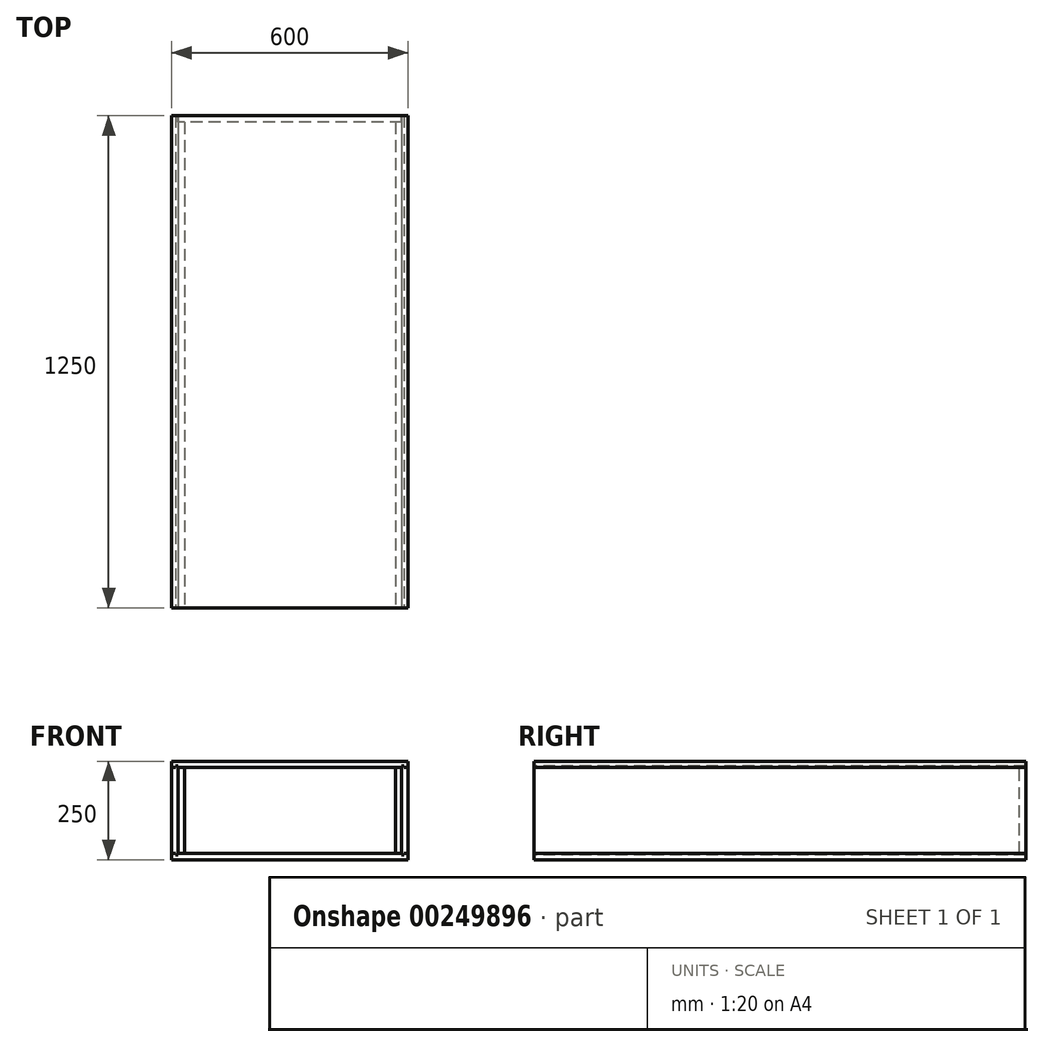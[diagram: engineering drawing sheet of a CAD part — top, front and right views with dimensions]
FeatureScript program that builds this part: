
annotation { "Feature Type Name" : "Feature", "Feature Type Description" : "" }
export const myFeature = defineFeature(function(context is Context, id is Id, definition is map)
    precondition{}
    {
        {
            var Q0;
            Q0=qCreatedBy(makeId("Front.planeOp"),FACE);
            var sketch = newSketch(context, id + "F0", { "sketchPlane" : qUnion([Q0])});
            skLineSegment(sketch, "E0.bottom", {"start": v(300, -125) * mm, "end": v(-300, -125) * mm});
            skLineSegment(sketch, "E0.top", {"start": v(300, 125) * mm, "end": v(-300, 125) * mm});
            skLineSegment(sketch, "E0.left", {"start": v(300, -125) * mm, "end": v(300, 125) * mm});
            skLineSegment(sketch, "E0.right", {"start": v(-300, -125) * mm, "end": v(-300, 125) * mm});
            skPoint(sketch, "E0.middle", {"position": v(0, 0) * mm});
            skLineSegment(sketch, "E1.0", {"start": v(284, 109) * mm, "end": v(-284, 109) * mm});
            skLineSegment(sketch, "E1.1", {"start": v(284, -109) * mm, "end": v(284, 109) * mm});
            skLineSegment(sketch, "E1.2", {"start": v(284, -109) * mm, "end": v(-284, -109) * mm});
            skLineSegment(sketch, "E1.3", {"start": v(-284, -109) * mm, "end": v(-284, 109) * mm});
            skLineSegment(sketch, "E2", {"start": v(284, -109) * mm, "end": v(284, -113) * mm});
            skLineSegment(sketch, "E3", {"start": v(284, -113) * mm, "end": v(290, -113) * mm});
            skLineSegment(sketch, "E4", {"start": v(290, -113) * mm, "end": v(290, -109) * mm});
            skLineSegment(sketch, "E5", {"start": v(290, -109) * mm, "end": v(300, -109) * mm});
            skLineSegment(sketch, "E6", {"start": v(284, 109) * mm, "end": v(284, 113) * mm});
            skLineSegment(sketch, "E7", {"start": v(284, 113) * mm, "end": v(290, 113) * mm});
            skLineSegment(sketch, "E8", {"start": v(290, 113) * mm, "end": v(290, 109) * mm});
            skLineSegment(sketch, "E9", {"start": v(290, 109) * mm, "end": v(300, 109) * mm});
            skLineSegment(sketch, "E10", {"start": v(-284, 109) * mm, "end": v(-284, 113) * mm});
            skLineSegment(sketch, "E11", {"start": v(-284, 113) * mm, "end": v(-290, 113) * mm});
            skLineSegment(sketch, "E12", {"start": v(-290, 113) * mm, "end": v(-290, 109) * mm});
            skLineSegment(sketch, "E13", {"start": v(-290, 109) * mm, "end": v(-300, 109) * mm});
            skLineSegment(sketch, "E14", {"start": v(-284, -109) * mm, "end": v(-284, -113) * mm});
            skLineSegment(sketch, "E15", {"start": v(-284, -113) * mm, "end": v(-290, -113) * mm});
            skLineSegment(sketch, "E16", {"start": v(-290, -113) * mm, "end": v(-290, -109) * mm});
            skLineSegment(sketch, "E17", {"start": v(-290, -109) * mm, "end": v(-300, -109) * mm});
            skLineSegment(sketch, "E18.0", {"start": v(268, -109) * mm, "end": v(268, 109) * mm});
            skLineSegment(sketch, "E19.0", {"start": v(-268, -109) * mm, "end": v(-268, 109) * mm});
            skSolve(sketch);
        }
        {
            var Q0;
            Q0=makeQuery(id+"F0.imprint","IMPRINT",FACE,{"disambiguationData":[TD([[makeQuery(id+"F0.imprint","IMPRINT",EDGE,{"derivedFrom":sQuery(id+"F0.wireOp",EDGE,"E1.1")}),-1.0]])]});
            extrude(context, id + "F1", {"entities" : qUnion([Q0]), "oppositeDirection" : true, "depth" : 1250 * mm});
        }
        {
            var Q0;
            {var subQ7=sQuery(id+"F0.wireOp",EDGE,"E0.top");Q0=makeQuery(id+"F0.imprint","IMPRINT",FACE,{"disambiguationData":[TD([[makeQuery(id+"F0.imprint","IMPRINT",EDGE,{"derivedFrom":subQ7}),1.0]])]});}
            extrude(context, id + "F2", {"entities" : qUnion([Q0]), "oppositeDirection" : true, "depth" : 1250 * mm});
        }
        {
            var Q0;
            Q0=makeQuery(id+"F0.imprint","IMPRINT",FACE,{"disambiguationData":[TD([[makeQuery(id+"F0.imprint","IMPRINT",EDGE,{"derivedFrom":sQuery(id+"F0.wireOp",EDGE,"E1.3")}),1.0]])]});
            extrude(context, id + "F3", {"entities" : qUnion([Q0]), "oppositeDirection" : true, "depth" : 1250 * mm});
        }
        {
            var Q0;
            {var subQ6=sQuery(id+"F0.wireOp",EDGE,"E0.bottom");Q0=makeQuery(id+"F0.imprint","IMPRINT",FACE,{"disambiguationData":[TD([[makeQuery(id+"F0.imprint","IMPRINT",EDGE,{"derivedFrom":subQ6}),-1.0]])]});}
            extrude(context, id + "F4", {"entities" : qUnion([Q0]), "oppositeDirection" : true, "depth" : 1250 * mm});
        }
        {
            var Q0;
            {var subQ0=sQuery(id+"F0.wireOp",EDGE,"E1.1");Q0=makeQuery(id+"F0.imprint","IMPRINT",FACE,{"disambiguationData":[TD([[makeQuery(id+"F0.imprint","IMPRINT",EDGE,{"derivedFrom":subQ0}),1.0]])]});}
            extrude(context, id + "F5", {"entities" : qUnion([Q0]), "oppositeDirection" : true, "depth" : 1234 * mm});
        }
        {
            var Q0;
            {var subQ0=sQuery(id+"F0.wireOp",EDGE,"E1.3");Q0=makeQuery(id+"F0.imprint","IMPRINT",FACE,{"disambiguationData":[TD([[makeQuery(id+"F0.imprint","IMPRINT",EDGE,{"derivedFrom":subQ0}),-1.0]])]});}
            extrude(context, id + "F6", {"entities" : qUnion([Q0]), "oppositeDirection" : true, "depth" : 1234 * mm});
        }
        {
            var Q0;
            Q0=makeQuery(id+"F4.opExtrude","CAP_FACE",FACE,{"disambiguationData":[OSD([sQuery(id+"F0.wireOp",EDGE,"E0.bottom"),sQuery(id+"F0.wireOp",EDGE,"E0.left"),sQuery(id+"F0.wireOp",EDGE,"E0.right"),sQuery(id+"F0.wireOp",EDGE,"E1.2"),sQuery(id+"F0.wireOp",EDGE,"E2"),sQuery(id+"F0.wireOp",EDGE,"E3"),sQuery(id+"F0.wireOp",EDGE,"E4"),sQuery(id+"F0.wireOp",EDGE,"E5"),sQuery(id+"F0.wireOp",EDGE,"E14"),sQuery(id+"F0.wireOp",EDGE,"E15"),sQuery(id+"F0.wireOp",EDGE,"E16"),sQuery(id+"F0.wireOp",EDGE,"E17")])],"isStart":false});
            var sketch = newSketch(context, id + "F7", { "sketchPlane" : qUnion([Q0])});
            skSolve(sketch);
        }
        {
            var Q0;
            Q0=makeQuery(id+"F7.imprint","IMPRINT",FACE,{"disambiguationData":[TD([[makeQuery(id+"F7.imprint","IMPRINT",EDGE,{"derivedFrom":makeQuery(id+"F4.opExtrude","CAP_EDGE",EDGE,{"disambiguationData":[OSD([sQuery(id+"F0.wireOp",EDGE,"E0.bottom")])],"isStart":false})}),1.0]])]});
            var sketch = newSketch(context, id + "F8", { "sketchPlane" : qUnion([Q0])});
            skLineSegment(sketch, "E20.bottom", {"start": v(284, -109) * mm, "end": v(-284, -109) * mm});
            skLineSegment(sketch, "E20.top", {"start": v(284, 109) * mm, "end": v(-284, 109) * mm});
            skLineSegment(sketch, "E20.left", {"start": v(284, -109) * mm, "end": v(284, 109) * mm});
            skLineSegment(sketch, "E20.right", {"start": v(-284, -109) * mm, "end": v(-284, 109) * mm});
            skSolve(sketch);
        }
        {
            var Q0;
            Q0=makeQuery(id+"F8.imprint","IMPRINT",FACE,{"disambiguationData":[TD([[makeQuery(id+"F8.imprint","IMPRINT",EDGE,{"derivedFrom":sQuery(id+"F8.wireOp",EDGE,"E20.bottom")}),1.0]])]});
            extrude(context, id + "F9", {"entities" : qUnion([Q0]), "oppositeDirection" : true, "depth" : 16 * mm});
        }
    });
